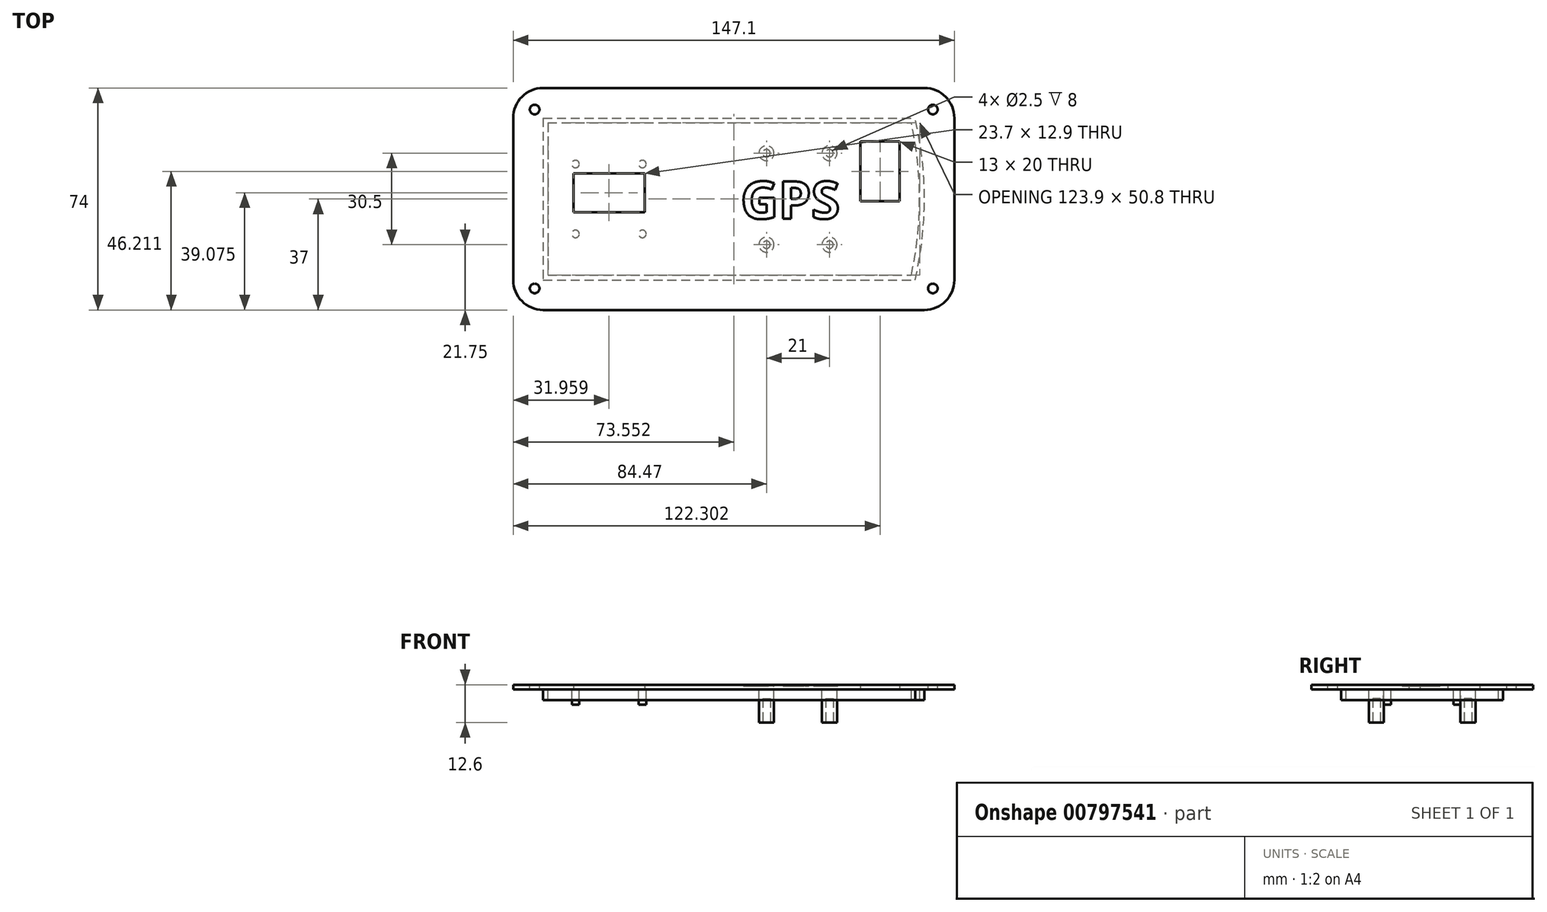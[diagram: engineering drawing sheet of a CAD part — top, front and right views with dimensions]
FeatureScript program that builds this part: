
annotation { "Feature Type Name" : "Feature", "Feature Type Description" : "" }
export const myFeature = defineFeature(function(context is Context, id is Id, definition is map)
    precondition{}
    {
        {
            var Q0;
            Q0=qCreatedBy(makeId("Top.planeOp"),FACE);
            var sketch = newSketch(context, id + "F0", { "sketchPlane" : qUnion([Q0])});
            skLineSegment(sketch, "E0.bottom", {"start": v(62, -27) * mm, "end": v(-62, -27) * mm, "construction": true});
            skLineSegment(sketch, "E0.top", {"start": v(62, 27) * mm, "end": v(-62, 27) * mm, "construction": true});
            skLineSegment(sketch, "E0.right", {"start": v(-62, -27) * mm, "end": v(-62, 27) * mm, "construction": true});
            skPoint(sketch, "E0.middle", {"position": v(0, 0) * mm});
            skArc(sketch, "E1", {"start": v(62, -27) * mm, "mid": v(65.1, 0) * mm, "end": v(62, 27) * mm, "construction": true});
            skPoint(sketch, "E2.oppositeSnap0", {"position": v(65.1, 0) * mm});
            skLineSegment(sketch, "E2.bottom", {"start": v(-62, 27) * mm, "end": v(62, 27) * mm});
            skLineSegment(sketch, "E2.top", {"start": v(-62, -27) * mm, "end": v(62, -27) * mm});
            skLineSegment(sketch, "E2.left", {"start": v(-62, 27) * mm, "end": v(-62, -27) * mm});
            skLineSegment(sketch, "E3.0", {"start": v(75.1, 37) * mm, "end": v(75.1, -37) * mm});
            skLineSegment(sketch, "E3.1", {"start": v(-72, 37) * mm, "end": v(75.1, 37) * mm});
            skLineSegment(sketch, "E3.2", {"start": v(-72, 37) * mm, "end": v(-72, -37) * mm});
            skLineSegment(sketch, "E3.3", {"start": v(-72, -37) * mm, "end": v(75.1, -37) * mm});
            skPoint(sketch, "E4.orphan", {"position": v(65.1, -27) * mm});
            skArc(sketch, "E5", {"start": v(62, -27) * mm, "mid": v(65.1, 0) * mm, "end": v(62, 27) * mm});
            skArc(sketch, "E6.0", {"start": v(60.72, -25.4) * mm, "mid": v(63.5, 0) * mm, "end": v(60.72, 25.4) * mm});
            skLineSegment(sketch, "E6.1", {"start": v(-60.4, -25.4) * mm, "end": v(60.72, -25.4) * mm});
            skLineSegment(sketch, "E6.2", {"start": v(-60.4, 25.4) * mm, "end": v(-60.4, -25.4) * mm});
            skLineSegment(sketch, "E6.3", {"start": v(-60.4, 25.4) * mm, "end": v(60.72, 25.4) * mm});
            skSolve(sketch);
        }
        {
            var Q0;
            Q0=makeQuery(id+"F0.imprint","IMPRINT",FACE,{"disambiguationData":[TD([[makeQuery(id+"F0.imprint","IMPRINT",EDGE,{"derivedFrom":sQuery(id+"F0.wireOp",EDGE,"E2.bottom")}),-1.0]])]});
            extrude(context, id + "F1", {"entities" : qUnion([Q0]), "oppositeDirection" : true, "depth" : 3.5 * mm, "offsetDistance" : 25 * mm});
        }
        {
            var Q0;
            Q0=makeQuery(id+"F0.imprint","IMPRINT",FACE,{"disambiguationData":[TD([[makeQuery(id+"F0.imprint","IMPRINT",EDGE,{"derivedFrom":sQuery(id+"F0.wireOp",EDGE,"E2.bottom")}),1.0]])]});
            var Q1;
            Q1=makeQuery(id+"F0.imprint","IMPRINT",FACE,{"disambiguationData":[TD([[makeQuery(id+"F0.imprint","IMPRINT",EDGE,{"derivedFrom":sQuery(id+"F0.wireOp",EDGE,"E6.0")}),1.0]])]});
            var Q2;
            Q2=makeQuery(id+"F0.imprint","IMPRINT",FACE,{"disambiguationData":[TD([[makeQuery(id+"F0.imprint","IMPRINT",EDGE,{"derivedFrom":sQuery(id+"F0.wireOp",EDGE,"E2.bottom")}),-1.0]])]});
            extrude(context, id + "F2", {"entities" : qUnion([Q0, Q1, Q2]), "depth" : 1.6 * mm, "offsetDistance" : 25 * mm});
        }
        {
            var Q0;
            Q0=makeQuery(id+"F0.imprint","IMPRINT",FACE,{"disambiguationData":[TD([[makeQuery(id+"F0.imprint","IMPRINT",EDGE,{"derivedFrom":sQuery(id+"F0.wireOp",EDGE,"E6.0")}),1.0]])]});
            var sketch = newSketch(context, id + "F3", { "sketchPlane" : qUnion([Q0])});
            skLineSegment(sketch, "E7.bottom", {"start": v(-26.4, 13.83) * mm, "end": v(-53.7, 13.83) * mm, "construction": true});
            skLineSegment(sketch, "E7.top", {"start": v(-26.4, -13.47) * mm, "end": v(-53.7, -13.47) * mm, "construction": true});
            skLineSegment(sketch, "E7.left", {"start": v(-26.4, 13.83) * mm, "end": v(-26.4, -13.47) * mm, "construction": true});
            skLineSegment(sketch, "E7.right", {"start": v(-53.7, 13.83) * mm, "end": v(-53.7, -13.47) * mm, "construction": true});
            skLineSegment(sketch, "E8.bottom", {"start": v(1.66, 22) * mm, "end": v(-18.34, 22) * mm, "construction": true});
            skLineSegment(sketch, "E8.top", {"start": v(1.66, -22) * mm, "end": v(-18.34, -22) * mm, "construction": true});
            skLineSegment(sketch, "E8.left", {"start": v(1.66, 22) * mm, "end": v(1.66, -22) * mm, "construction": true});
            skLineSegment(sketch, "E8.right", {"start": v(-18.34, 22) * mm, "end": v(-18.34, -22) * mm, "construction": true});
            skPoint(sketch, "E8.middle", {"position": v(-8.34, 0) * mm});
            skLineSegment(sketch, "E9.bottom", {"start": v(35.97, 18) * mm, "end": v(9.97, 18) * mm, "construction": true});
            skLineSegment(sketch, "E9.top", {"start": v(35.97, -18) * mm, "end": v(9.97, -18) * mm, "construction": true});
            skLineSegment(sketch, "E9.left", {"start": v(35.97, 18) * mm, "end": v(35.97, -18) * mm, "construction": true});
            skLineSegment(sketch, "E9.right", {"start": v(9.97, 18) * mm, "end": v(9.97, -18) * mm, "construction": true});
            skPoint(sketch, "E9.middle", {"position": v(22.97, 0) * mm});
            skLineSegment(sketch, "E10.bottom", {"start": v(57.8, 19.71) * mm, "end": v(42.8, 19.71) * mm, "construction": true});
            skLineSegment(sketch, "E10.top", {"start": v(57.8, -1.29) * mm, "end": v(42.8, -1.29) * mm, "construction": true});
            skLineSegment(sketch, "E10.left", {"start": v(57.8, 19.71) * mm, "end": v(57.8, -1.29) * mm, "construction": true});
            skLineSegment(sketch, "E10.right", {"start": v(42.8, 19.71) * mm, "end": v(42.8, -1.29) * mm, "construction": true});
            skPoint(sketch, "E10.middle", {"position": v(50.3, 9.21) * mm});
            skLineSegment(sketch, "E11.bottom", {"start": v(-28.9, 11.65) * mm, "end": v(-51.2, 11.65) * mm, "construction": true});
            skLineSegment(sketch, "E11.top", {"start": v(-28.9, -11.65) * mm, "end": v(-51.2, -11.65) * mm, "construction": true});
            skLineSegment(sketch, "E11.left", {"start": v(-28.9, 11.65) * mm, "end": v(-28.9, -11.65) * mm, "construction": true});
            skLineSegment(sketch, "E11.right", {"start": v(-51.2, 11.65) * mm, "end": v(-51.2, -11.65) * mm, "construction": true});
            skPoint(sketch, "E11.middle", {"position": v(-40.04, 0) * mm});
            skLineSegment(sketch, "E12.bottom", {"start": v(-26.4, 9.63) * mm, "end": v(-53.7, 9.63) * mm, "construction": true});
            skLineSegment(sketch, "E12.top", {"start": v(-26.4, -9.63) * mm, "end": v(-53.7, -9.63) * mm, "construction": true});
            skLineSegment(sketch, "E12.left", {"start": v(-26.4, 9.63) * mm, "end": v(-26.4, -9.63) * mm, "construction": true});
            skLineSegment(sketch, "E12.right", {"start": v(-53.7, 9.63) * mm, "end": v(-53.7, -9.63) * mm, "construction": true});
            skLineSegment(sketch, "E13", {"start": v(-40.04, -13.47) * mm, "end": v(-40.04, 13.83) * mm, "construction": true});
            skCircle(sketch, "E14", {"center": v(-28.9, -11.65) * mm, "radius": 1.25 * mm});
            skCircle(sketch, "E15", {"center": v(-51.2, -11.65) * mm, "radius": 1.25 * mm});
            skCircle(sketch, "E16", {"center": v(-28.9, 11.65) * mm, "radius": 1.25 * mm});
            skCircle(sketch, "E17", {"center": v(-51.2, 11.65) * mm, "radius": 1.25 * mm});
            skLineSegment(sketch, "E18.bottom", {"start": v(-28.2, 8.53) * mm, "end": v(-51.9, 8.53) * mm, "construction": true});
            skLineSegment(sketch, "E18.top", {"start": v(-28.2, -4.37) * mm, "end": v(-51.9, -4.37) * mm, "construction": true});
            skLineSegment(sketch, "E18.left", {"start": v(-28.2, 8.53) * mm, "end": v(-28.2, -4.37) * mm, "construction": true});
            skLineSegment(sketch, "E18.right", {"start": v(-51.9, 8.53) * mm, "end": v(-51.9, -4.38) * mm, "construction": true});
            skPoint(sketch, "E18.middle", {"position": v(-40.04, 2.08) * mm});
            skLineSegment(sketch, "E19.bottom", {"start": v(-51.9, -4.37) * mm, "end": v(-28.2, -4.37) * mm});
            skLineSegment(sketch, "E19.top", {"start": v(-51.9, 8.53) * mm, "end": v(-28.2, 8.53) * mm});
            skLineSegment(sketch, "E19.left", {"start": v(-51.9, -4.37) * mm, "end": v(-51.9, 8.53) * mm});
            skLineSegment(sketch, "E19.right", {"start": v(-28.2, -4.37) * mm, "end": v(-28.2, 8.53) * mm});
            skLineSegment(sketch, "E20.bottom", {"start": v(56.8, 19.21) * mm, "end": v(43.8, 19.21) * mm});
            skLineSegment(sketch, "E20.top", {"start": v(56.8, -0.79) * mm, "end": v(43.8, -0.79) * mm});
            skLineSegment(sketch, "E20.left", {"start": v(56.8, 19.21) * mm, "end": v(56.8, -0.79) * mm});
            skLineSegment(sketch, "E20.right", {"start": v(43.8, 19.21) * mm, "end": v(43.8, -0.79) * mm});
            skLineSegment(sketch, "E21.bottom", {"start": v(33.47, 15.25) * mm, "end": v(12.47, 15.25) * mm, "construction": true});
            skLineSegment(sketch, "E21.top", {"start": v(33.47, -15.25) * mm, "end": v(12.47, -15.25) * mm, "construction": true});
            skLineSegment(sketch, "E21.left", {"start": v(33.47, 15.25) * mm, "end": v(33.47, -15.25) * mm, "construction": true});
            skLineSegment(sketch, "E21.right", {"start": v(12.47, 15.25) * mm, "end": v(12.47, -15.25) * mm, "construction": true});
            skCircle(sketch, "E22", {"center": v(12.47, -15.25) * mm, "radius": 2.5 * mm});
            skCircle(sketch, "E23", {"center": v(33.47, -15.25) * mm, "radius": 2.5 * mm});
            skCircle(sketch, "E24", {"center": v(12.47, 15.25) * mm, "radius": 2.5 * mm});
            skCircle(sketch, "E25", {"center": v(33.47, 15.25) * mm, "radius": 2.5 * mm});
            skSolve(sketch);
        }
        {
            var Q0;
            Q0=makeQuery(id+"F3.imprint","IMPRINT",FACE,{"disambiguationData":[TD([[makeQuery(id+"F3.imprint","IMPRINT",EDGE,{"derivedFrom":sQuery(id+"F3.wireOp",EDGE,"E19.bottom")}),1.0]])]});
            var Q1;
            Q1=makeQuery(id+"F3.imprint","IMPRINT",FACE,{"disambiguationData":[TD([[makeQuery(id+"F3.imprint","IMPRINT",EDGE,{"derivedFrom":sQuery(id+"F3.wireOp",EDGE,"E20.bottom")}),1.0]])]});
            extrude(context, id + "F4", {"entities" : qUnion([Q0, Q1]), "operationType" : NewBodyOperationType.REMOVE, "endBound" : BoundingType.THROUGH_ALL, "depth" : 25 * mm, "offsetDistance" : 25 * mm});
        }
        {
            var Q0;
            Q0=makeQuery(id+"F3.imprint","IMPRINT",FACE,{"disambiguationData":[TD([[makeQuery(id+"F3.imprint","IMPRINT",EDGE,{"derivedFrom":sQuery(id+"F3.wireOp",EDGE,"E15")}),1.0]])]});
            var Q1;
            Q1=makeQuery(id+"F3.imprint","IMPRINT",FACE,{"disambiguationData":[TD([[makeQuery(id+"F3.imprint","IMPRINT",EDGE,{"derivedFrom":sQuery(id+"F3.wireOp",EDGE,"E14")}),1.0]])]});
            var Q2;
            Q2=makeQuery(id+"F3.imprint","IMPRINT",FACE,{"disambiguationData":[TD([[makeQuery(id+"F3.imprint","IMPRINT",EDGE,{"derivedFrom":sQuery(id+"F3.wireOp",EDGE,"E16")}),1.0]])]});
            var Q3;
            Q3=makeQuery(id+"F3.imprint","IMPRINT",FACE,{"disambiguationData":[TD([[makeQuery(id+"F3.imprint","IMPRINT",EDGE,{"derivedFrom":sQuery(id+"F3.wireOp",EDGE,"E17")}),1.0]])]});
            var Q4;
            Q4=sQuery(id+"F3.wireOp",EDGE,"E14");
            var Q5;
            Q5=sQuery(id+"F3.wireOp",EDGE,"E16");
            var Q6;
            Q6=sQuery(id+"F3.wireOp",EDGE,"E17");
            var Q7;
            Q7=sQuery(id+"F3.wireOp",EDGE,"E15");
            extrude(context, id + "F5", {"entities" : qUnion([Q0, Q1, Q2, Q3]), "surfaceEntities" : qUnion([Q4, Q5, Q6, Q7]), "oppositeDirection" : true, "depth" : 5 * mm, "offsetDistance" : 25 * mm});
        }
        {
            var Q0;
            Q0=makeQuery(id+"F3.imprint","IMPRINT",FACE,{"disambiguationData":[TD([[makeQuery(id+"F3.imprint","IMPRINT",EDGE,{"derivedFrom":sQuery(id+"F3.wireOp",EDGE,"E24")}),1.0]])]});
            var Q1;
            Q1=makeQuery(id+"F3.imprint","IMPRINT",FACE,{"disambiguationData":[TD([[makeQuery(id+"F3.imprint","IMPRINT",EDGE,{"derivedFrom":sQuery(id+"F3.wireOp",EDGE,"E25")}),1.0]])]});
            var Q2;
            Q2=makeQuery(id+"F3.imprint","IMPRINT",FACE,{"disambiguationData":[TD([[makeQuery(id+"F3.imprint","IMPRINT",EDGE,{"derivedFrom":sQuery(id+"F3.wireOp",EDGE,"E23")}),1.0]])]});
            var Q3;
            Q3=makeQuery(id+"F3.imprint","IMPRINT",FACE,{"disambiguationData":[TD([[makeQuery(id+"F3.imprint","IMPRINT",EDGE,{"derivedFrom":sQuery(id+"F3.wireOp",EDGE,"E22")}),1.0]])]});
            var Q4;
            Q4=sQuery(id+"F3.wireOp",EDGE,"E22");
            var Q5;
            Q5=sQuery(id+"F3.wireOp",EDGE,"E23");
            var Q6;
            Q6=sQuery(id+"F3.wireOp",EDGE,"E25");
            var Q7;
            Q7=sQuery(id+"F3.wireOp",EDGE,"E24");
            extrude(context, id + "F6", {"entities" : qUnion([Q0, Q1, Q2, Q3]), "surfaceEntities" : qUnion([Q4, Q5, Q6, Q7]), "oppositeDirection" : true, "depth" : 11 * mm, "offsetDistance" : 25 * mm});
        }
        {
            var Q0;
            Q0=makeQuery(id+"F2.opExtrude","SWEPT_EDGE",EDGE,{"disambiguationData":[OSD([sQuery(id+"F0.wireOp",EDGE,"E3.0"),sQuery(id+"F0.wireOp",EDGE,"E3.1")])]});
            var Q1;
            Q1=makeQuery(id+"F2.opExtrude","SWEPT_EDGE",EDGE,{"disambiguationData":[OSD([sQuery(id+"F0.wireOp",EDGE,"E3.1"),sQuery(id+"F0.wireOp",EDGE,"E3.2")])]});
            var Q2;
            Q2=makeQuery(id+"F2.opExtrude","SWEPT_EDGE",EDGE,{"disambiguationData":[OSD([sQuery(id+"F0.wireOp",EDGE,"E3.2"),sQuery(id+"F0.wireOp",EDGE,"E3.3")])]});
            var Q3;
            Q3=makeQuery(id+"F2.opExtrude","SWEPT_EDGE",EDGE,{"disambiguationData":[OSD([sQuery(id+"F0.wireOp",EDGE,"E3.0"),sQuery(id+"F0.wireOp",EDGE,"E3.3")])]});
            fillet(context, id + "F7", {"entities" : qUnion([Q0, Q1, Q2, Q3]), "radius" : 10 * mm, "tangentPropagation" : true, "allowEdgeOverflow" : false});
        }
        {
            var Q0;
            Q0=makeQuery(id+"F6.opExtrude","CAP_FACE",FACE,{"disambiguationData":[OSD([sQuery(id+"F3.wireOp",EDGE,"E22")])],"isStart":false});
            var sketch = newSketch(context, id + "F8", { "sketchPlane" : qUnion([Q0])});
            skCircle(sketch, "E26", {"center": v(12.47, 15.25) * mm, "radius": 1.25 * mm});
            skSolve(sketch);
        }
        {
            var Q0;
            Q0 = qSketchRegion(id + "F8", true);
            extrude(context, id + "F9", {"entities" : qUnion([Q0]), "operationType" : NewBodyOperationType.REMOVE, "oppositeDirection" : true, "depth" : 8 * mm, "offsetDistance" : 25 * mm});
        }
        {
            var Q0;
            Q0=makeQuery(id+"F6.opExtrude","CAP_FACE",FACE,{"disambiguationData":[OSD([sQuery(id+"F3.wireOp",EDGE,"E23")])],"isStart":false});
            var sketch = newSketch(context, id + "F10", { "sketchPlane" : qUnion([Q0])});
            skCircle(sketch, "E27", {"center": v(33.47, 15.25) * mm, "radius": 1.25 * mm});
            skSolve(sketch);
        }
        {
            var Q0;
            Q0 = qSketchRegion(id + "F10", true);
            extrude(context, id + "F11", {"entities" : qUnion([Q0]), "operationType" : NewBodyOperationType.REMOVE, "oppositeDirection" : true, "depth" : 8 * mm, "offsetDistance" : 25 * mm});
        }
        {
            var Q0;
            Q0=makeQuery(id+"F6.opExtrude","CAP_FACE",FACE,{"disambiguationData":[OSD([sQuery(id+"F3.wireOp",EDGE,"E24")])],"isStart":false});
            var sketch = newSketch(context, id + "F12", { "sketchPlane" : qUnion([Q0])});
            skCircle(sketch, "E28", {"center": v(12.47, -15.25) * mm, "radius": 1.25 * mm});
            skSolve(sketch);
        }
        {
            var Q0;
            Q0 = qSketchRegion(id + "F12", true);
            extrude(context, id + "F13", {"entities" : qUnion([Q0]), "operationType" : NewBodyOperationType.REMOVE, "oppositeDirection" : true, "depth" : 8 * mm, "offsetDistance" : 25 * mm});
        }
        {
            var Q0;
            Q0=makeQuery(id+"F6.opExtrude","CAP_FACE",FACE,{"disambiguationData":[OSD([sQuery(id+"F3.wireOp",EDGE,"E25")])],"isStart":false});
            var sketch = newSketch(context, id + "F14", { "sketchPlane" : qUnion([Q0])});
            skCircle(sketch, "E29", {"center": v(33.47, -15.25) * mm, "radius": 1.25 * mm});
            skSolve(sketch);
        }
        {
            var Q0;
            Q0 = qSketchRegion(id + "F14", true);
            extrude(context, id + "F15", {"entities" : qUnion([Q0]), "operationType" : NewBodyOperationType.REMOVE, "oppositeDirection" : true, "depth" : 8 * mm, "offsetDistance" : 25 * mm});
        }
        {
            var Q0;
            Q0=makeQuery(id+"F2.opExtrude","CAP_FACE",FACE,{"disambiguationData":[OSD([sQuery(id+"F0.wireOp",EDGE,"E3.0"),sQuery(id+"F0.wireOp",EDGE,"E3.1"),sQuery(id+"F0.wireOp",EDGE,"E3.2"),sQuery(id+"F0.wireOp",EDGE,"E3.3")])],"isStart":false});
            var sketch = newSketch(context, id + "F16", { "sketchPlane" : qUnion([Q0])});
            skArc(sketch, "E30.0", {"start": v(-62, 31) * mm, "mid": v(-64.83, 29.83) * mm, "end": v(-66, 27) * mm, "construction": true});
            skLineSegment(sketch, "E30.1", {"start": v(65.1, 31) * mm, "end": v(-62, 31) * mm, "construction": true});
            skLineSegment(sketch, "E30.2", {"start": v(-66, 27) * mm, "end": v(-66, -27) * mm, "construction": true});
            skArc(sketch, "E30.3", {"start": v(69.1, 27) * mm, "mid": v(67.93, 29.83) * mm, "end": v(65.1, 31) * mm, "construction": true});
            skArc(sketch, "E30.4", {"start": v(-66, -27) * mm, "mid": v(-64.83, -29.83) * mm, "end": v(-62, -31) * mm, "construction": true});
            skLineSegment(sketch, "E30.5", {"start": v(-62, -31) * mm, "end": v(65.1, -31) * mm, "construction": true});
            skArc(sketch, "E30.6", {"start": v(65.1, -31) * mm, "mid": v(67.93, -29.83) * mm, "end": v(69.1, -27) * mm, "construction": true});
            skLineSegment(sketch, "E30.7", {"start": v(69.1, -27) * mm, "end": v(69.1, 27) * mm, "construction": true});
            skCircle(sketch, "E31", {"center": v(-64.83, 29.83) * mm, "radius": 1.6 * mm});
            skCircle(sketch, "E32", {"center": v(67.93, 29.83) * mm, "radius": 1.6 * mm});
            skCircle(sketch, "E33", {"center": v(-64.83, -29.83) * mm, "radius": 1.6 * mm});
            skCircle(sketch, "E34", {"center": v(67.93, -29.83) * mm, "radius": 1.6 * mm});
            skSolve(sketch);
        }
        {
            var Q0;
            Q0 = qSketchRegion(id + "F16", true);
            extrude(context, id + "F17", {"entities" : qUnion([Q0]), "operationType" : NewBodyOperationType.REMOVE, "endBound" : BoundingType.THROUGH_ALL, "oppositeDirection" : true, "depth" : 25 * mm, "offsetDistance" : 25 * mm});
        }
        {
            var Q0;
            Q0=makeQuery(id+"F2.opExtrude","CAP_FACE",FACE,{"disambiguationData":[OSD([sQuery(id+"F0.wireOp",EDGE,"E3.0"),sQuery(id+"F0.wireOp",EDGE,"E3.1"),sQuery(id+"F0.wireOp",EDGE,"E3.2"),sQuery(id+"F0.wireOp",EDGE,"E3.3")])],"isStart":false});
            var sketch = newSketch(context, id + "F18", { "sketchPlane" : qUnion([Q0])});
            skSolve(sketch);
        }
        {
            var Q0;
            {var subQ3=sQuery(id+"F0.wireOp",EDGE,"E3.0");Q0=makeQuery(id+"F18.imprint","IMPRINT",FACE,{"disambiguationData":[TD([[makeQuery(id+"F18.imprint","IMPRINT",EDGE,{"derivedFrom":makeQuery(id+"F2.opExtrude","CAP_EDGE",EDGE,{"disambiguationData":[OSD([subQ3])],"isStart":false})}),-1.0]])]});}
            var sketch = newSketch(context, id + "F19", { "sketchPlane" : qUnion([Q0])});
            skText(sketch, "E35", { "text": "GPS", "fontName": "OpenSans-Bold.ttf"});
            const initialGuessF19  = {"E35": [0.00382, -0.0066, 1, 0, 0.01253]};
            skSetInitialGuess(sketch, initialGuessF19);
            skSolve(sketch);
        }
        {
            var Q0;
            Q0 = qSketchRegion(id + "F19", true);
            extrude(context, id + "F20", {"entities" : qUnion([Q0]), "operationType" : NewBodyOperationType.REMOVE, "oppositeDirection" : true, "depth" : 0.4 * mm, "offsetDistance" : 25 * mm});
        }
    });
